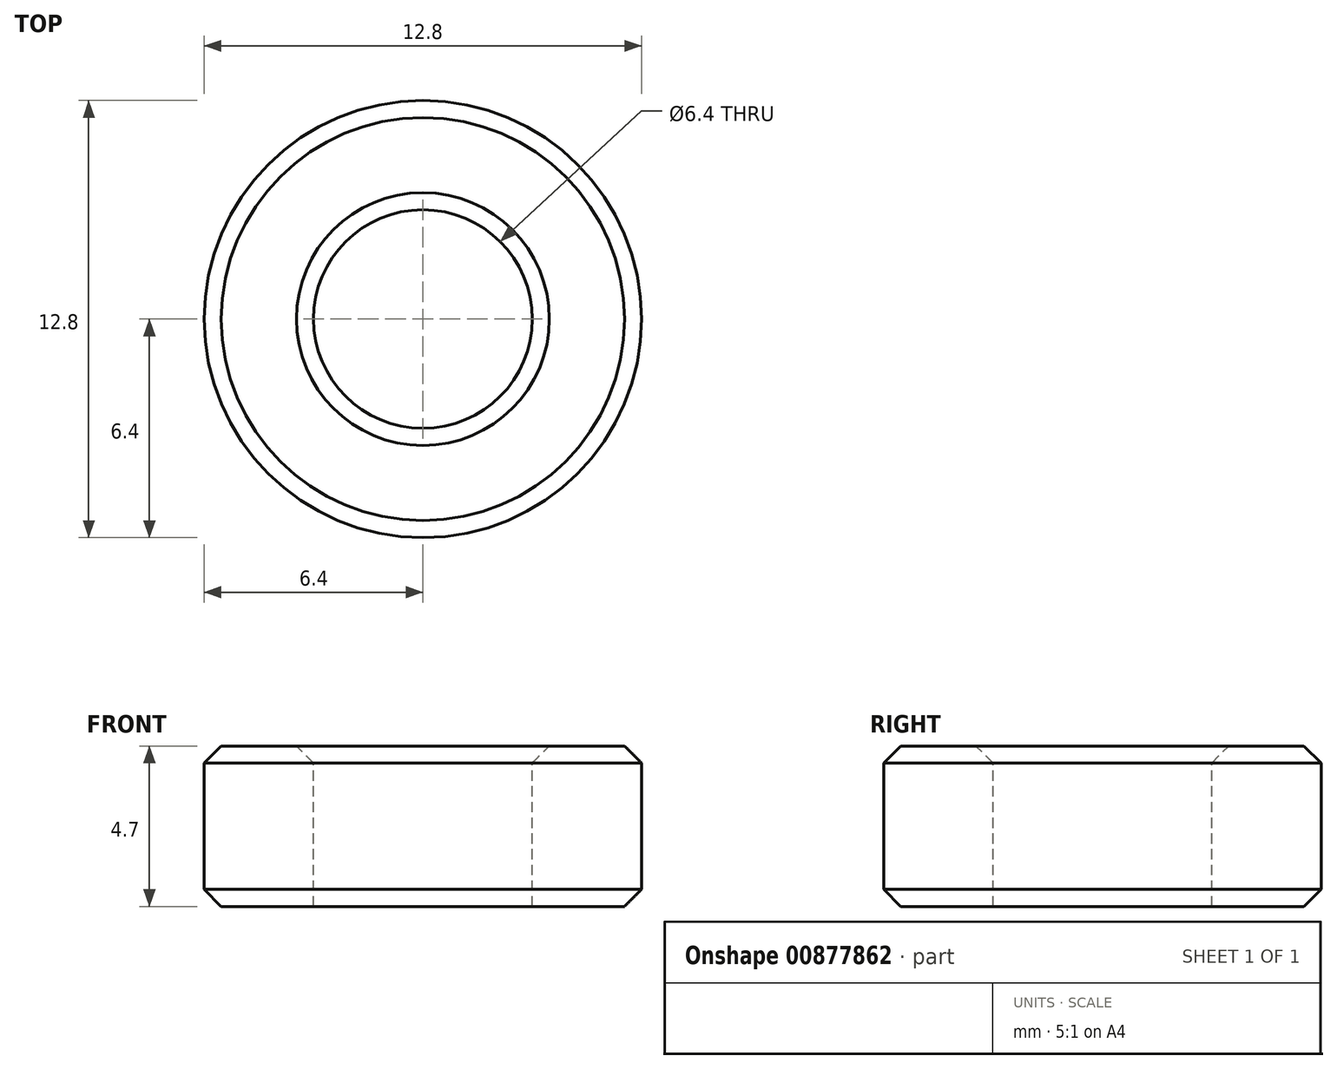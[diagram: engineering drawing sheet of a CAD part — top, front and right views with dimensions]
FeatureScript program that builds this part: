
annotation { "Feature Type Name" : "Feature", "Feature Type Description" : "" }
export const myFeature = defineFeature(function(context is Context, id is Id, definition is map)
    precondition{}
    {
        {
            var Q0;
            Q0=qCreatedBy(makeId("Top.planeOp"),FACE);
            var sketch = newSketch(context, id + "F0", { "sketchPlane" : qUnion([Q0])});
            skCircle(sketch, "E0", {"center": v(0, 0) * mm, "radius": 6.4 * mm});
            skSolve(sketch);
        }
        {
            var Q0;
            Q0 = qSketchRegion(id + "F0", true);
            extrude(context, id + "F1", {"entities" : qUnion([Q0]), "depth" : 4.7 * mm, "offsetDistance" : 25 * mm});
        }
        {
            var Q0;
            Q0=makeQuery(id+"F1.opExtrude","CAP_FACE",FACE,{"disambiguationData":[OSD([sQuery(id+"F0.wireOp",EDGE,"E0")])],"isStart":false});
            var sketch = newSketch(context, id + "F2", { "sketchPlane" : qUnion([Q0])});
            skCircle(sketch, "E1", {"center": v(0, 0) * mm, "radius": 3.2 * mm});
            skSolve(sketch);
        }
        {
            var Q0;
            Q0=makeQuery(id+"F2.imprint","IMPRINT",FACE,{"disambiguationData":[TD([[makeQuery(id+"F2.imprint","IMPRINT",EDGE,{"derivedFrom":sQuery(id+"F2.wireOp",EDGE,"E1")}),1.0]])]});
            extrude(context, id + "F3", {"entities" : qUnion([Q0]), "operationType" : NewBodyOperationType.REMOVE, "oppositeDirection" : true, "depth" : 25 * mm, "offsetDistance" : 25 * mm});
        }
        {
            var Q0;
            Q0=makeQuery(id+"F1.opExtrude","CAP_FACE",FACE,{"disambiguationData":[OSD([sQuery(id+"F0.wireOp",EDGE,"E0")])],"isStart":false});
            chamfer(context, id + "F4", {"entities" : qUnion([Q0]), "width" : 0.5 * mm, "tangentPropagation" : true});
        }
        {
            var Q0;
            Q0=makeQuery(id+"F1.opExtrude","CAP_EDGE",EDGE,{"disambiguationData":[OSD([sQuery(id+"F0.wireOp",EDGE,"E0")])],"isStart":true});
            chamfer(context, id + "F5", {"entities" : qUnion([Q0]), "width" : 0.5 * mm, "tangentPropagation" : true});
        }
    });
